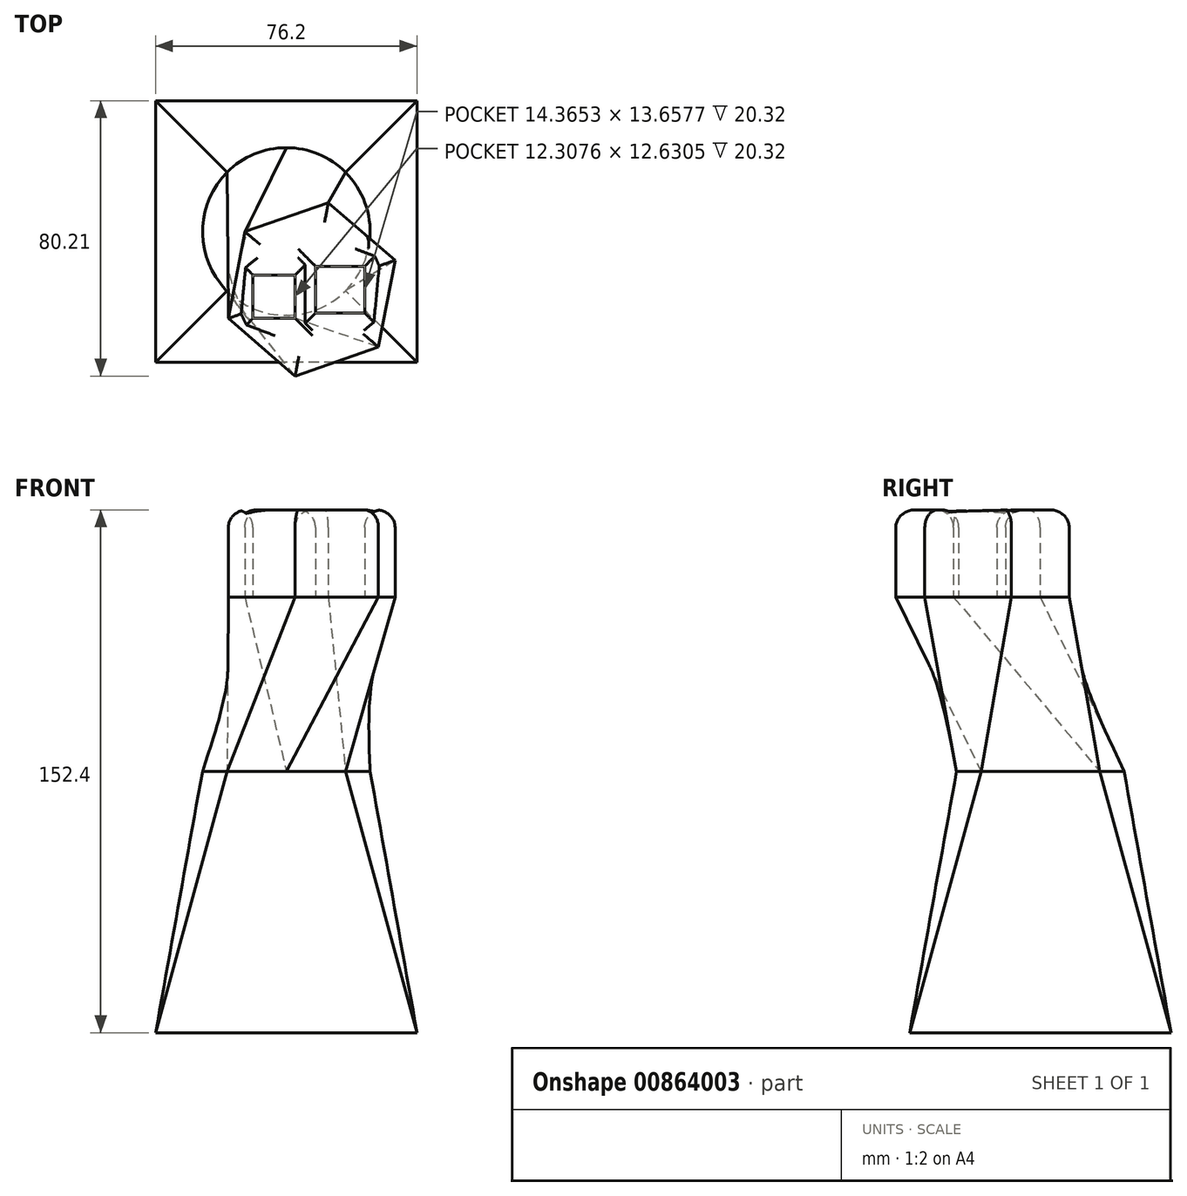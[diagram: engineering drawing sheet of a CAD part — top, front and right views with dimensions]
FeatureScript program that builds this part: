
annotation { "Feature Type Name" : "Feature", "Feature Type Description" : "" }
export const myFeature = defineFeature(function(context is Context, id is Id, definition is map)
    precondition{}
    {
        {
            var Q0;
            Q0=qCreatedBy(makeId("Top.planeOp"),FACE);
            var sketch = newSketch(context, id + "F0", { "sketchPlane" : qUnion([Q0])});
            skLineSegment(sketch, "E0.bottom", {"start": v(38.1, 38.1) * mm, "end": v(-38.1, 38.1) * mm});
            skLineSegment(sketch, "E0.top", {"start": v(38.1, -38.1) * mm, "end": v(-38.1, -38.1) * mm});
            skLineSegment(sketch, "E0.left", {"start": v(38.1, 38.1) * mm, "end": v(38.1, -38.1) * mm});
            skLineSegment(sketch, "E0.right", {"start": v(-38.1, 38.1) * mm, "end": v(-38.1, -38.1) * mm});
            skPoint(sketch, "E0.middle", {"position": v(0, 0) * mm});
            skSolve(sketch);
        }
        {
            var Q0;
            Q0=makeQuery(id+"F0.imprint","IMPRINT",FACE,{"disambiguationData":[TD([[makeQuery(id+"F0.imprint","IMPRINT",EDGE,{"derivedFrom":sQuery(id+"F0.wireOp",EDGE,"E0.bottom")}),1.0]])]});
            cPlane(context, id + "F1", {"entities" : qUnion([Q0]), "cplaneType" : CPlaneType.OFFSET, "offset" : 76.2 * mm, "width" : 152.4 * mm, "height" : 152.4 * mm});
        }
        {
            var Q0;
            Q0=qCreatedBy(id+"F1.planeOp",FACE);
            var sketch = newSketch(context, id + "F2", { "sketchPlane" : qUnion([Q0])});
            skCircle(sketch, "E1", {"center": v(0, 0) * mm, "radius": 24.43 * mm});
            skSolve(sketch);
        }
        {
            var Q0;
            Q0=makeQuery(id+"F0.imprint","IMPRINT",FACE,{"disambiguationData":[TD([[makeQuery(id+"F0.imprint","IMPRINT",EDGE,{"derivedFrom":sQuery(id+"F0.wireOp",EDGE,"E0.bottom")}),1.0]])]});
            var Q1;
            Q1=makeQuery(id+"F2.imprint","IMPRINT",FACE,{"disambiguationData":[TD([[makeQuery(id+"F2.imprint","IMPRINT",EDGE,{"derivedFrom":sQuery(id+"F2.wireOp",EDGE,"E1")}),1.0]])]});
            loft(context, id + "F3", {"sheetProfilesArray" : [{ "sheetProfileEntities" : qUnion([Q0]) }, { "sheetProfileEntities" : qUnion([Q1]) }]});
        }
        {
            var Q0;
            Q0=qCreatedBy(id+"F1.planeOp",FACE);
            cPlane(context, id + "F4", {"entities" : qUnion([Q0]), "cplaneType" : CPlaneType.OFFSET, "offset" : 50.8 * mm, "width" : 152.4 * mm, "height" : 152.4 * mm});
        }
        {
            var Q0;
            Q0=qCreatedBy(id+"F4.planeOp",FACE);
            var sketch = newSketch(context, id + "F5", { "sketchPlane" : qUnion([Q0])});
            skCircle(sketch, "E2.cCircle", {"center": v(7.42, -16.85) * mm, "radius": 22.27 * mm, "construction": true});
            skLineSegment(sketch, "E2.0", {"start": v(12.26, 8.41) * mm, "end": v(31.71, -8.41) * mm});
            skLineSegment(sketch, "E2.1", {"start": v(31.71, -8.41) * mm, "end": v(26.87, -33.67) * mm});
            skLineSegment(sketch, "E2.2", {"start": v(26.87, -33.67) * mm, "end": v(2.58, -42.11) * mm});
            skLineSegment(sketch, "E2.3", {"start": v(2.58, -42.11) * mm, "end": v(-16.88, -25.3) * mm});
            skLineSegment(sketch, "E2.4", {"start": v(-16.88, -25.3) * mm, "end": v(-12.04, -0.03) * mm});
            skLineSegment(sketch, "E2.5", {"start": v(-12.04, -0.03) * mm, "end": v(12.26, 8.41) * mm});
            skPoint(sketch, "E2.0.midPoint", {"position": v(21.98, 0) * mm});
            skSolve(sketch);
        }
        {
            var Q1;
            Q1=makeQuery(id+"F5.imprint","IMPRINT",FACE,{"disambiguationData":[TD([[makeQuery(id+"F5.imprint","IMPRINT",EDGE,{"derivedFrom":sQuery(id+"F5.wireOp",EDGE,"E2.0")}),-1.0]])]});
            var Q2;
            Q2=makeQuery(id+"F3.opLoft","CAP_FACE",FACE,{"disambiguationData":[OSD([makeQuery(id+"F2.imprint","IMPRINT",FACE,{"disambiguationData":[TD([[makeQuery(id+"F2.imprint","IMPRINT",EDGE,{"derivedFrom":sQuery(id+"F2.wireOp",EDGE,"E1")}),1.0]])]})])],"isStart":true});
            loft(context, id + "F6", {"operationType" : NewBodyOperationType.ADD, "sheetProfilesArray" : [{ "sheetProfileEntities" : qUnion([Q1]) }, { "sheetProfileEntities" : qUnion([Q2]) }]});
        }
        {
            var Q0;
            Q0=makeQuery(id+"F6.opLoft","CAP_FACE",FACE,{"disambiguationData":[OSD([makeQuery(id+"F5.imprint","IMPRINT",FACE,{"disambiguationData":[TD([[makeQuery(id+"F5.imprint","IMPRINT",EDGE,{"derivedFrom":sQuery(id+"F5.wireOp",EDGE,"E2.0")}),-1.0]])]})])],"isStart":true});
            var sketch = newSketch(context, id + "F7", { "sketchPlane" : qUnion([Q0])});
            skLineSegment(sketch, "E3.bottom", {"start": v(8.5, -23.77) * mm, "end": v(22.87, -23.77) * mm});
            skLineSegment(sketch, "E3.top", {"start": v(8.5, -10.12) * mm, "end": v(22.87, -10.12) * mm});
            skLineSegment(sketch, "E3.left", {"start": v(8.5, -23.77) * mm, "end": v(8.5, -10.12) * mm});
            skLineSegment(sketch, "E3.right", {"start": v(22.87, -23.77) * mm, "end": v(22.87, -10.12) * mm});
            skPoint(sketch, "E4.firstSnap0", {"position": v(-14.46, -12.66) * mm});
            skLineSegment(sketch, "E4.bottom", {"start": v(-9.73, -12.66) * mm, "end": v(2.58, -12.66) * mm});
            skLineSegment(sketch, "E4.top", {"start": v(-9.73, -25.3) * mm, "end": v(2.58, -25.3) * mm});
            skLineSegment(sketch, "E4.left", {"start": v(-9.73, -12.66) * mm, "end": v(-9.73, -25.3) * mm});
            skLineSegment(sketch, "E4.right", {"start": v(2.58, -12.66) * mm, "end": v(2.58, -25.3) * mm});
            skSolve(sketch);
        }
        {
            var Q0;
            Q0=makeQuery(id+"F7.imprint","IMPRINT",FACE,{"disambiguationData":[TD([[makeQuery(id+"F7.imprint","IMPRINT",EDGE,{"derivedFrom":sQuery(id+"F7.wireOp",EDGE,"E3.bottom")}),-1.0]])]});
            extrude(context, id + "F8", {"entities" : qUnion([Q0]), "operationType" : NewBodyOperationType.ADD, "depth" : 25.4 * mm, "offsetDistance" : 25.4 * mm});
        }
        {
            var Q0;
            Q0=makeQuery(id+"F8.opExtrude","CAP_FACE",FACE,{"disambiguationData":[OSD([sQuery(id+"F5.wireOp",EDGE,"E2.0"),sQuery(id+"F5.wireOp",EDGE,"E2.1"),sQuery(id+"F5.wireOp",EDGE,"E2.2"),sQuery(id+"F5.wireOp",EDGE,"E2.3"),sQuery(id+"F5.wireOp",EDGE,"E2.4"),sQuery(id+"F5.wireOp",EDGE,"E2.5"),sQuery(id+"F7.wireOp",EDGE,"E3.bottom"),sQuery(id+"F7.wireOp",EDGE,"E3.top"),sQuery(id+"F7.wireOp",EDGE,"E3.left"),sQuery(id+"F7.wireOp",EDGE,"E3.right"),sQuery(id+"F7.wireOp",EDGE,"E4.bottom"),sQuery(id+"F7.wireOp",EDGE,"E4.top"),sQuery(id+"F7.wireOp",EDGE,"E4.left"),sQuery(id+"F7.wireOp",EDGE,"E4.right")])],"isStart":false});
            fillet(context, id + "F9", {"entities" : qUnion([Q0]), "radius" : 5.08 * mm, "tangentPropagation" : true, "allowEdgeOverflow" : false});
        }
    });
